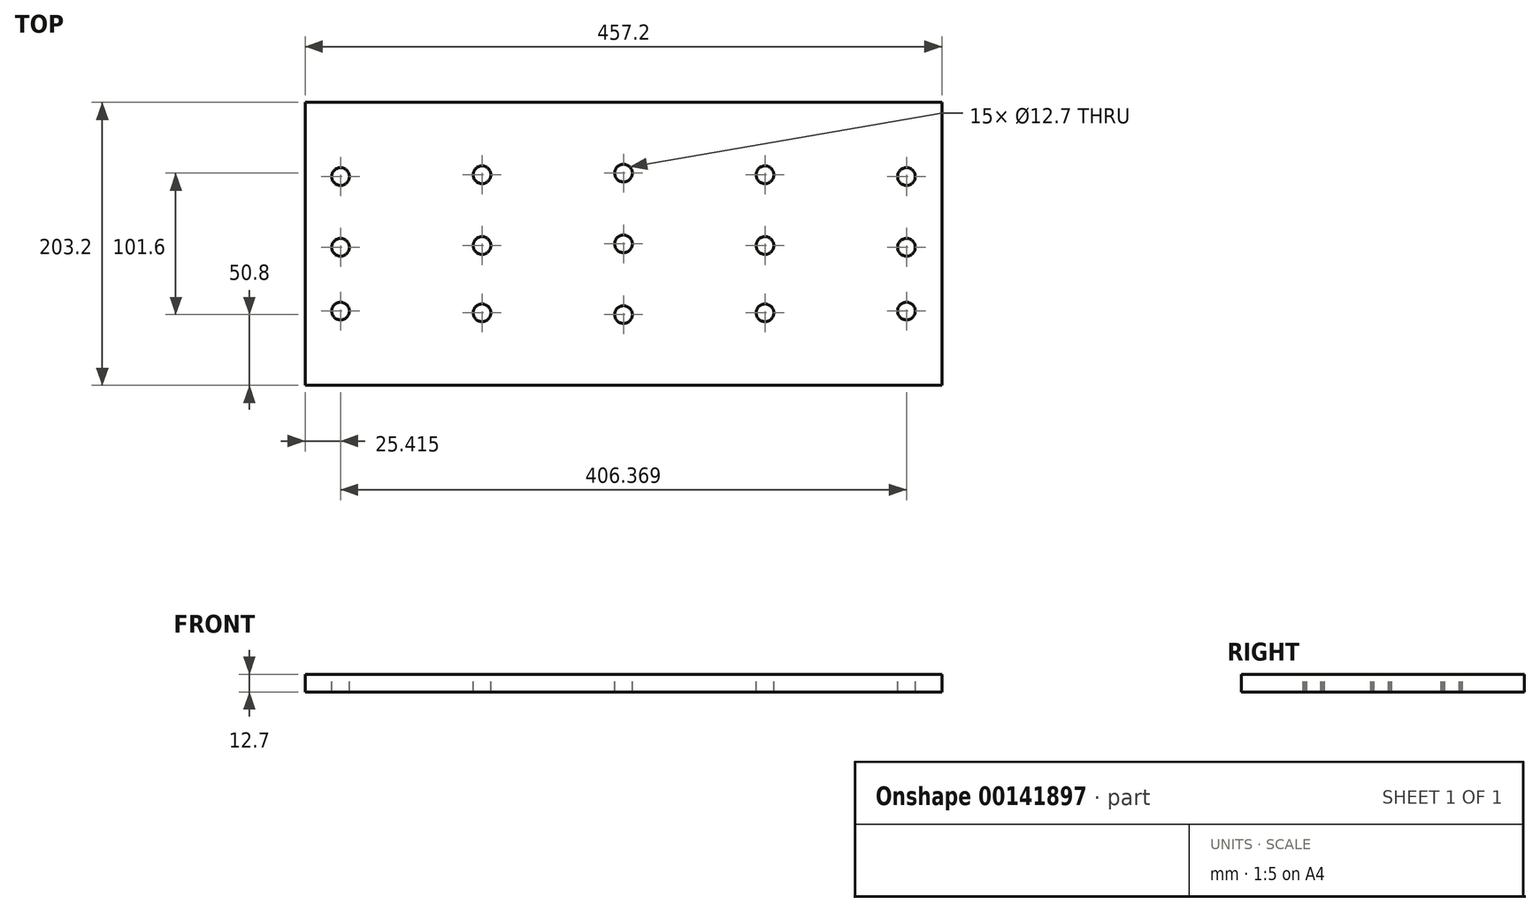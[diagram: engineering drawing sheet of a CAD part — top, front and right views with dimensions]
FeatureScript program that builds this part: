
annotation { "Feature Type Name" : "Feature", "Feature Type Description" : "" }
export const myFeature = defineFeature(function(context is Context, id is Id, definition is map)
    precondition{}
    {
        {
            var Q0;
            Q0=qCreatedBy(makeId("Top.planeOp"),FACE);
            var sketch = newSketch(context, id + "F0", { "sketchPlane" : qUnion([Q0])});
            skLineSegment(sketch, "E0.bottom", {"start": v(-228.6, -101.6) * mm, "end": v(228.6, -101.6) * mm});
            skLineSegment(sketch, "E0.top", {"start": v(-228.6, 101.6) * mm, "end": v(228.6, 101.6) * mm});
            skLineSegment(sketch, "E0.left", {"start": v(-228.6, -101.6) * mm, "end": v(-228.6, 101.6) * mm});
            skLineSegment(sketch, "E0.right", {"start": v(228.6, -101.6) * mm, "end": v(228.6, 101.6) * mm});
            skPoint(sketch, "E0.middle", {"position": v(0, 0) * mm});
            skSolve(sketch);
        }
        {
            var Q0;
            Q0=makeQuery(id+"F0.imprint","IMPRINT",FACE,{"disambiguationData":[TD([[makeQuery(id+"F0.imprint","IMPRINT",EDGE,{"derivedFrom":sQuery(id+"F0.wireOp",EDGE,"E0.bottom")}),1.0]])]});
            extrude(context, id + "F1", {"entities" : qUnion([Q0]), "oppositeDirection" : true, "depth" : 12.7 * mm});
        }
        {
            var Q0;
            Q0=makeQuery(id+"F1.opExtrude","CAP_FACE",FACE,{"disambiguationData":[OSD([sQuery(id+"F0.wireOp",EDGE,"E0.bottom"),sQuery(id+"F0.wireOp",EDGE,"E0.top"),sQuery(id+"F0.wireOp",EDGE,"E0.left"),sQuery(id+"F0.wireOp",EDGE,"E0.right")])],"isStart":true});
            var sketch = newSketch(context, id + "F2", { "sketchPlane" : qUnion([Q0])});
            skLineSegment(sketch, "E1.bottom", {"start": v(-66.04, -114.3) * mm, "end": v(66.04, -114.3) * mm, "construction": true});
            skLineSegment(sketch, "E1.top", {"start": v(-66.04, 114.3) * mm, "end": v(66.04, 114.3) * mm, "construction": true});
            skLineSegment(sketch, "E1.left", {"start": v(-66.04, -114.3) * mm, "end": v(-66.04, 114.3) * mm, "construction": true});
            skLineSegment(sketch, "E1.right", {"start": v(66.04, -114.3) * mm, "end": v(66.04, 114.3) * mm, "construction": true});
            skPoint(sketch, "E1.middle", {"position": v(0, 0) * mm});
            skCircle(sketch, "E2", {"center": v(0, 0) * mm, "radius": 6.35 * mm});
            skCircle(sketch, "E3.0.1.0", {"center": v(0, 50.8) * mm, "radius": 6.35 * mm});
            skCircle(sketch, "E3.1.0.0", {"center": v(101.6, -1.25) * mm, "radius": 6.35 * mm});
            skCircle(sketch, "E3.1.1.0", {"center": v(101.6, 49.55) * mm, "radius": 6.35 * mm});
            skCircle(sketch, "E3.2.0.0", {"center": v(203.18, -2.5) * mm, "radius": 6.35 * mm});
            skCircle(sketch, "E3.2.1.0", {"center": v(203.18, 48.3) * mm, "radius": 6.35 * mm});
            skLineSegment(sketch, "E3.direction1", {"start": v(0, 0) * mm, "end": v(101.6, -1.25) * mm, "construction": true});
            skLineSegment(sketch, "E3.direction2", {"start": v(0, 0) * mm, "end": v(0, 50.8) * mm, "construction": true});
            skCircle(sketch, "E4.MirrorC", {"center": v(101.6, -49.55) * mm, "radius": 6.35 * mm});
            skCircle(sketch, "E5.MirrorC", {"center": v(203.18, -48.3) * mm, "radius": 6.35 * mm});
            skCircle(sketch, "E6.MirrorC", {"center": v(0, -50.8) * mm, "radius": 6.35 * mm});
            skCircle(sketch, "E7.MirrorC", {"center": v(-101.6, -1.25) * mm, "radius": 6.35 * mm});
            skCircle(sketch, "E8.MirrorC", {"center": v(-101.6, -49.55) * mm, "radius": 6.35 * mm});
            skCircle(sketch, "E9.MirrorC", {"center": v(-203.18, -48.3) * mm, "radius": 6.35 * mm});
            skCircle(sketch, "E10.MirrorC", {"center": v(-101.6, 49.55) * mm, "radius": 6.35 * mm});
            skCircle(sketch, "E11.MirrorC", {"center": v(-203.18, -2.5) * mm, "radius": 6.35 * mm});
            skCircle(sketch, "E12.MirrorC", {"center": v(-203.18, 48.3) * mm, "radius": 6.35 * mm});
            skLineSegment(sketch, "E13.bottom", {"start": v(-177.8, -95.25) * mm, "end": v(177.8, -95.25) * mm, "construction": true});
            skLineSegment(sketch, "E13.top", {"start": v(-177.8, 95.25) * mm, "end": v(177.8, 95.25) * mm, "construction": true});
            skLineSegment(sketch, "E13.left", {"start": v(-177.8, -95.25) * mm, "end": v(-177.8, 95.25) * mm, "construction": true});
            skLineSegment(sketch, "E13.right", {"start": v(177.8, -95.25) * mm, "end": v(177.8, 95.25) * mm, "construction": true});
            skSolve(sketch);
        }
        {
            var Q0;
            Q0 = qSketchRegion(id + "F2", true);
            extrude(context, id + "F3", {"entities" : qUnion([Q0]), "operationType" : NewBodyOperationType.REMOVE, "oppositeDirection" : true, "depth" : 25.4 * mm});
        }
    });
